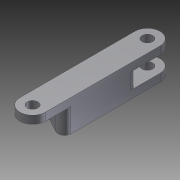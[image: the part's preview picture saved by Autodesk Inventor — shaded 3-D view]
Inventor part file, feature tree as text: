
AUTODESK INVENTOR PART (.ipt)
format: ipt  version: 2011 SP2 (Build 150309200, 309)  size: 131,072 bytes
history: native  units: mm
features: sketch x3, extrude x3, hole x1, fillet x1
ambient origin geometry x8: Origin, YZ Plane, XZ Plane, XY Plane, X Axis, Y Axis, Z Axis, Center Point
feature tree (8):
  sketch  "Sketch1"  dims[d0=4.0mm d6=38.1mm]
  extrude  "Extrusion5"  Depth=38.1mm
  extrude  "Extrusion6"  Depth=5.0mm TaperAngle=0.0deg
  hole  "Hole3"  [1 undecoded]
  fillet  "Fillet1"  Radius=10.0mm
  extrude  "Extrusion7"  [1 undecoded]
  sketch  "Sketch4"  dims[d36=10.0mm d37=0.0mm d38=5.0mm d39=0.0mm]
  sketch  "Sketch5"  dims[d40=3.4mm d41=6.0mm d42=4.4mm d43=3.0mm d44=90.0deg d45=8.0mm d46=20.594885mm d47=2.0mm d48=10.0mm d49=0.0mm]
note: 2 required parameter values undecoded (feature->parameter linkage not recoverable at this tier; creation-order binding heuristic only, values carry confidence <= 0.55)
